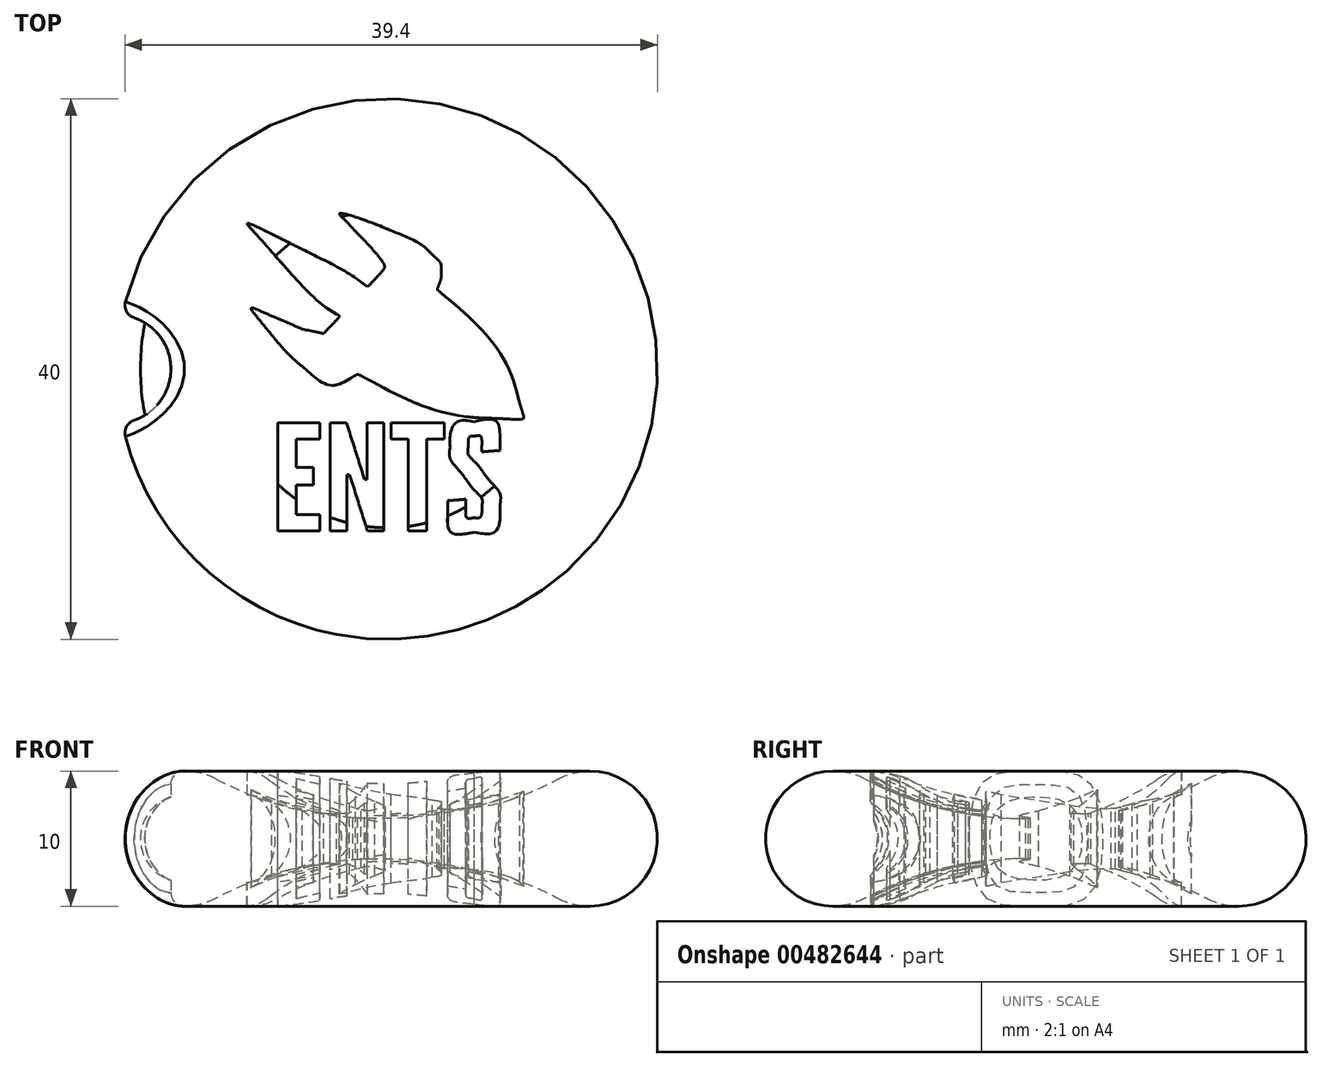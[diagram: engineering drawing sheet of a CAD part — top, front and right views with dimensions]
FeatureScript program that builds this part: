
annotation { "Feature Type Name" : "Feature", "Feature Type Description" : "" }
export const myFeature = defineFeature(function(context is Context, id is Id, definition is map)
    precondition{}
    {
        {
            var Q0;
            Q0=qCreatedBy(makeId("Front.planeOp"),FACE);
            var sketch = newSketch(context, id + "F0", { "sketchPlane" : qUnion([Q0])});
            skArc(sketch, "E0", {"start": v(-12.65, 5.91) * mm, "mid": v(-20, 1.5) * mm, "end": v(-12.65, -2.91) * mm});
            skArc(sketch, "E1", {"start": v(-12.65, 5.91) * mm, "mid": v(-6.52, 3.62) * mm, "end": v(0, 3) * mm});
            skLineSegment(sketch, "E2", {"start": v(0, 1.5) * mm, "end": v(-20, 1.5) * mm, "construction": true});
            skArc(sketch, "E3.MirrorCS", {"start": v(-12.65, -2.91) * mm, "mid": v(-6.52, -0.62) * mm, "end": v(0, 0) * mm});
            skLineSegment(sketch, "E4", {"start": v(0, 3) * mm, "end": v(0, 0) * mm});
            skSolve(sketch);
        }
        {
            var Q0;
            Q0=makeQuery(id+"F0.imprint","IMPRINT",FACE,{"disambiguationData":[TD([[makeQuery(id+"F0.imprint","IMPRINT",EDGE,{"derivedFrom":sQuery(id+"F0.wireOp",EDGE,"E0")}),1.0]])]});
            var Q1;
            Q1=sQuery(id+"F0.wireOp",EDGE,"E4");
            revolve(context, id + "F1", {"entities" : qUnion([Q0]), "axis" : qUnion([Q1]), "revolveType" : RevolveType.FULL});
        }
        {
            var Q0;
            Q0=qCreatedBy(makeId("Top.planeOp"),FACE);
            var sketch = newSketch(context, id + "F2", { "sketchPlane" : qUnion([Q0])});
            skCircle(sketch, "E5", {"center": v(-20, 0) * mm, "radius": 4 * mm});
            skSolve(sketch);
        }
        {
            var Q0;
            Q0=makeQuery(id+"F2.imprint","IMPRINT",FACE,{"disambiguationData":[TD([[makeQuery(id+"F2.imprint","IMPRINT",EDGE,{"derivedFrom":sQuery(id+"F2.wireOp",EDGE,"E5")}),1.0]])]});
            extrude(context, id + "F3", {"entities" : qUnion([Q0]), "operationType" : NewBodyOperationType.REMOVE, "endBound" : BoundingType.SYMMETRIC, "depth" : 25 * mm});
        }
        {
            var Q0;
            Q0=makeQuery(id+"F3.boolean.opBoolean","INTERSECT",EDGE,{"derivedFrom":[makeQuery(id+"F1.opRevolve","SWEPT_FACE",FACE,{"disambiguationData":[OSD([sQuery(id+"F0.wireOp",EDGE,"E0")])]}),makeQuery(id+"F3.opExtrude","SWEPT_FACE",FACE,{"disambiguationData":[OSD([sQuery(id+"F2.wireOp",EDGE,"E5")])]})]});
            fillet(context, id + "F4", {"entities" : qUnion([Q0]), "radius" : 1 * mm, "tangentPropagation" : true, "allowEdgeOverflow" : false});
        }
        {
            var Q0;
            Q0=qCreatedBy(makeId("Top.planeOp"),FACE);
            cPlane(context, id + "F5", {"entities" : qUnion([Q0]), "cplaneType" : CPlaneType.OFFSET, "offset" : 10 * mm, "width" : 150 * mm, "height" : 150 * mm});
        }
        {
            var Q0;
            Q0=qCreatedBy(id+"F5.planeOp",FACE);
            var sketch = newSketch(context, id + "F6", { "sketchPlane" : qUnion([Q0])});
            skFitSpline(sketch, "E6", {"points": [v(6.26, -0.16) * mm, v(5.7, -0.77) * mm, v(4.66, -0.87) * mm, v(3.96, -0.38) * mm], "construction": true});
            skFitSpline(sketch, "E7", {"points": [v(3.96, -0.38) * mm, v(3.25, 0.1) * mm, v(3.14, 1) * mm, v(3.7, 1.6) * mm], "construction": true});
            skFitSpline(sketch, "E8", {"points": [v(3.7, 1.6) * mm, v(4.26, 2.21) * mm, v(5.3, 2.31) * mm, v(6, 1.82) * mm], "construction": true});
            skFitSpline(sketch, "E9", {"points": [v(6, 1.82) * mm, v(6.7, 1.34) * mm, v(6.82, 0.45) * mm, v(6.26, -0.16) * mm], "construction": true});
            skLineSegment(sketch, "E10", {"start": v(-8.08, -3.99) * mm, "end": v(-4.97, -3.99) * mm});
            skLineSegment(sketch, "E11", {"start": v(-4.97, -3.99) * mm, "end": v(-4.97, -5.2) * mm});
            skLineSegment(sketch, "E12", {"start": v(-4.97, -5.2) * mm, "end": v(-6.72, -5.2) * mm});
            skLineSegment(sketch, "E13", {"start": v(-6.72, -5.2) * mm, "end": v(-6.72, -7.3) * mm});
            skLineSegment(sketch, "E14", {"start": v(-6.72, -7.3) * mm, "end": v(-5.46, -7.3) * mm});
            skLineSegment(sketch, "E15", {"start": v(-5.46, -7.3) * mm, "end": v(-5.46, -8.58) * mm});
            skLineSegment(sketch, "E16", {"start": v(-5.46, -8.58) * mm, "end": v(-6.72, -8.58) * mm});
            skLineSegment(sketch, "E17", {"start": v(-6.72, -8.58) * mm, "end": v(-6.72, -10.78) * mm});
            skLineSegment(sketch, "E18", {"start": v(-6.72, -10.78) * mm, "end": v(-4.97, -10.78) * mm});
            skLineSegment(sketch, "E19", {"start": v(-4.97, -10.78) * mm, "end": v(-4.97, -11.99) * mm});
            skLineSegment(sketch, "E20", {"start": v(-4.97, -11.99) * mm, "end": v(-8.08, -11.99) * mm});
            skLineSegment(sketch, "E21", {"start": v(-8.08, -11.99) * mm, "end": v(-8.08, -3.99) * mm});
            skLineSegment(sketch, "E22", {"start": v(-2.96, -7.82) * mm, "end": v(-2.96, -11.99) * mm});
            skLineSegment(sketch, "E23", {"start": v(-2.96, -11.99) * mm, "end": v(-4.21, -11.99) * mm});
            skLineSegment(sketch, "E24", {"start": v(-4.21, -11.99) * mm, "end": v(-4.21, -3.99) * mm});
            skLineSegment(sketch, "E25", {"start": v(-4.21, -3.99) * mm, "end": v(-3, -3.99) * mm});
            skLineSegment(sketch, "E26", {"start": v(-3, -3.99) * mm, "end": v(-1.68, -8.16) * mm});
            skLineSegment(sketch, "E27", {"start": v(-1.49, -8.16) * mm, "end": v(-1.49, -3.99) * mm});
            skLineSegment(sketch, "E28", {"start": v(-1.49, -3.99) * mm, "end": v(-0.24, -3.99) * mm});
            skLineSegment(sketch, "E29", {"start": v(-0.24, -3.99) * mm, "end": v(-0.24, -11.99) * mm});
            skLineSegment(sketch, "E30", {"start": v(-0.24, -11.99) * mm, "end": v(-1.45, -11.99) * mm});
            skLineSegment(sketch, "E31", {"start": v(-1.45, -11.99) * mm, "end": v(-2.77, -7.82) * mm});
            skFitSpline(sketch, "E32", {"points": [v(6.44, -3.9) * mm, v(8.08, -3.87) * mm, v(8.35, -5.13) * mm, v(8.35, -6.02) * mm]});
            skLineSegment(sketch, "E33", {"start": v(0.29, -5.2) * mm, "end": v(0.29, -3.99) * mm});
            skLineSegment(sketch, "E34", {"start": v(0.29, -3.99) * mm, "end": v(4.22, -3.99) * mm});
            skLineSegment(sketch, "E35", {"start": v(4.22, -3.99) * mm, "end": v(4.22, -5.2) * mm});
            skLineSegment(sketch, "E36", {"start": v(4.22, -5.2) * mm, "end": v(2.94, -5.2) * mm});
            skLineSegment(sketch, "E37", {"start": v(2.94, -5.2) * mm, "end": v(2.94, -11.99) * mm});
            skLineSegment(sketch, "E38", {"start": v(2.94, -11.99) * mm, "end": v(1.58, -11.99) * mm});
            skLineSegment(sketch, "E39", {"start": v(1.58, -11.99) * mm, "end": v(1.58, -5.2) * mm});
            skLineSegment(sketch, "E40", {"start": v(1.58, -5.2) * mm, "end": v(0.29, -5.2) * mm});
            skFitSpline(sketch, "E41", {"points": [v(7, -6.13) * mm, v(7, -5.6) * mm, v(6.92, -4.98) * mm, v(6.47, -4.98) * mm]});
            skFitSpline(sketch, "E42", {"points": [v(6.47, -4.98) * mm, v(6.11, -5) * mm, v(6, -5.32) * mm, v(6, -5.77) * mm]});
            skFitSpline(sketch, "E43", {"points": [v(6, -5.77) * mm, v(6, -6.32) * mm, v(6.54, -6.93) * mm, v(7.07, -7.6) * mm]});
            skFitSpline(sketch, "E44", {"points": [v(7.07, -7.6) * mm, v(7.7, -8.4) * mm, v(8.35, -9.2) * mm, v(8.35, -10.06) * mm]});
            skFitSpline(sketch, "E45", {"points": [v(8.35, -10.06) * mm, v(8.35, -11.13) * mm, v(7.94, -12.08) * mm, v(6.46, -12.08) * mm]});
            skFitSpline(sketch, "E46", {"points": [v(6.46, -12.08) * mm, v(4.7, -12.08) * mm, v(4.48, -10.93) * mm, v(4.48, -9.75) * mm]});
            skLineSegment(sketch, "E47", {"start": v(8.35, -6.02) * mm, "end": v(7, -6.13) * mm});
            skFitSpline(sketch, "E48", {"points": [v(5.81, -9.64) * mm, v(5.81, -10.3) * mm, v(5.89, -11) * mm, v(6.46, -11) * mm]});
            skFitSpline(sketch, "E49", {"points": [v(6.46, -11) * mm, v(6.86, -11) * mm, v(7.01, -10.62) * mm, v(7.01, -10.12) * mm]});
            skFitSpline(sketch, "E50", {"points": [v(7.01, -10.12) * mm, v(7.01, -9.58) * mm, v(6.43, -8.94) * mm, v(5.91, -8.27) * mm]});
            skFitSpline(sketch, "E51", {"points": [v(5.91, -8.27) * mm, v(5.27, -7.45) * mm, v(4.66, -6.63) * mm, v(4.66, -5.77) * mm]});
            skFitSpline(sketch, "E52", {"points": [v(4.66, -5.77) * mm, v(4.66, -4.9) * mm, v(5.16, -3.92) * mm, v(6.44, -3.9) * mm]});
            skLineSegment(sketch, "E53", {"start": v(4.48, -9.75) * mm, "end": v(5.81, -9.64) * mm});
            skLineSegment(sketch, "E54", {"start": v(-2.96, -7.82) * mm, "end": v(-2.77, -7.82) * mm});
            skLineSegment(sketch, "E55", {"start": v(-1.68, -8.16) * mm, "end": v(-1.49, -8.16) * mm});
            skSolve(sketch);
        }
        {
            var Q0;
            Q0 = qSketchRegion(id + "F6", true);
            extrude(context, id + "F7", {"entities" : qUnion([Q0]), "operationType" : NewBodyOperationType.REMOVE, "oppositeDirection" : true, "depth" : 25 * mm});
        }
        {
            var Q0;
            Q0=qCreatedBy(id+"F5.planeOp",FACE);
            var sketch = newSketch(context, id + "F8", { "sketchPlane" : qUnion([Q0])});
            skFitSpline(sketch, "E56", {"points": [v(-3.48, 11.5) * mm, v(-3.5, 11.51) * mm, v(-3.52, 11.5) * mm, v(-3.53, 11.5) * mm]});
            skFitSpline(sketch, "E57", {"points": [v(-3.53, 11.5) * mm, v(-3.54, 11.49) * mm, v(-3.01, 10.9) * mm, v(-2.35, 10.2) * mm]});
            skFitSpline(sketch, "E58", {"points": [v(-2.35, 10.2) * mm, v(-1.69, 9.5) * mm, v(-1.04, 8.8) * mm, v(-0.9, 8.65) * mm]});
            skFitSpline(sketch, "E59", {"points": [v(-0.9, 8.65) * mm, v(-0.66, 8.37) * mm, v(-0.17, 7.59) * mm, v(-0.2, 7.51) * mm]});
            skFitSpline(sketch, "E60", {"points": [v(-0.2, 7.51) * mm, v(-0.22, 7.43) * mm, v(-1.43, 6.13) * mm, v(-1.48, 6.13) * mm]});
            skFitSpline(sketch, "E61", {"points": [v(-1.48, 6.13) * mm, v(-1.5, 6.13) * mm, v(-1.7, 6.26) * mm, v(-1.93, 6.42) * mm]});
            skFitSpline(sketch, "E62", {"points": [v(-1.93, 6.42) * mm, v(-2.67, 6.96) * mm, v(-4.18, 7.81) * mm, v(-6.1, 8.77) * mm]});
            skFitSpline(sketch, "E63", {"points": [v(-6.1, 8.77) * mm, v(-7.7, 9.57) * mm, v(-10.25, 10.78) * mm, v(-10.34, 10.78) * mm]});
            skFitSpline(sketch, "E64", {"points": [v(-10.34, 10.78) * mm, v(-10.38, 10.78) * mm, v(-9.65, 9.92) * mm, v(-8.6, 8.73) * mm]});
            skFitSpline(sketch, "E65", {"points": [v(-8.6, 8.73) * mm, v(-6.63, 6.53) * mm, v(-4.68, 4.65) * mm, v(-3.73, 4.06) * mm]});
            skFitSpline(sketch, "E66", {"points": [v(-3.73, 4.06) * mm, v(-3.63, 4) * mm, v(-3.54, 3.92) * mm, v(-3.54, 3.9) * mm]});
            skFitSpline(sketch, "E67", {"points": [v(-3.54, 3.9) * mm, v(-3.54, 3.86) * mm, v(-3.8, 3.56) * mm, v(-4.12, 3.23) * mm]});
            skFitSpline(sketch, "E68", {"points": [v(-5.5, 2.8) * mm, v(-6.26, 2.96) * mm, v(-6.36, 3) * mm, v(-8.14, 3.76) * mm]});
            skFitSpline(sketch, "E69", {"points": [v(-8.14, 3.76) * mm, v(-9.16, 4.2) * mm, v(-10, 4.54) * mm, v(-10.03, 4.53) * mm]});
            skFitSpline(sketch, "E70", {"points": [v(-10.03, 4.53) * mm, v(-10.08, 4.52) * mm, v(-9.22, 3.35) * mm, v(-8.53, 2.5) * mm]});
            skFitSpline(sketch, "E71", {"points": [v(-8.53, 2.5) * mm, v(-7.83, 1.66) * mm, v(-6.86, 0.66) * mm, v(-6.28, 0.2) * mm]});
            skFitSpline(sketch, "E72", {"points": [v(-6.28, 0.2) * mm, v(-4.8, -1) * mm, v(-3.8, -1.19) * mm, v(-2.52, -0.56) * mm]});
            skLineSegment(sketch, "E73", {"start": v(-4.12, 3.23) * mm, "end": v(-4.7, 2.62) * mm});
            skLineSegment(sketch, "E74", {"start": v(-4.7, 2.62) * mm, "end": v(-5.5, 2.8) * mm});
            skFitSpline(sketch, "E75", {"points": [v(-1.43, -0.76) * mm, v(1.95, -2.45) * mm, v(5.3, -3.46) * mm, v(8.27, -3.66) * mm]});
            skFitSpline(sketch, "E76", {"points": [v(8.27, -3.66) * mm, v(8.93, -3.7) * mm, v(10.03, -3.7) * mm, v(10.07, -3.66) * mm]});
            skFitSpline(sketch, "E77", {"points": [v(10.07, -3.66) * mm, v(10.1, -3.62) * mm, v(9.98, -3.1) * mm, v(9.8, -2.55) * mm]});
            skFitSpline(sketch, "E78", {"points": [v(9.8, -2.55) * mm, v(8.96, 0.1) * mm, v(6.9, 3) * mm, v(4.05, 5.58) * mm]});
            skLineSegment(sketch, "E79", {"start": v(-2.52, -0.56) * mm, "end": v(-2.17, -0.39) * mm});
            skLineSegment(sketch, "E80", {"start": v(-2.17, -0.39) * mm, "end": v(-1.43, -0.76) * mm});
            skFitSpline(sketch, "E81", {"points": [v(3.85, 6.3) * mm, v(3.97, 6.62) * mm, v(4, 6.78) * mm, v(4, 7.12) * mm]});
            skFitSpline(sketch, "E82", {"points": [v(4, 7.12) * mm, v(4, 7.69) * mm, v(3.86, 7.96) * mm, v(3.34, 8.46) * mm]});
            skFitSpline(sketch, "E83", {"points": [v(3.34, 8.46) * mm, v(2.7, 9.07) * mm, v(1.73, 9.64) * mm, v(0.3, 10.24) * mm]});
            skFitSpline(sketch, "E84", {"points": [v(0.3, 10.24) * mm, v(-0.88, 10.72) * mm, v(-3.14, 11.48) * mm, v(-3.48, 11.5) * mm]});
            skLineSegment(sketch, "E85", {"start": v(4.05, 5.58) * mm, "end": v(3.7, 5.9) * mm});
            skLineSegment(sketch, "E86", {"start": v(3.7, 5.9) * mm, "end": v(3.85, 6.3) * mm});
            skFitSpline(sketch, "E87", {"points": [v(4.4, 1.47) * mm, v(5.03, 1.51) * mm, v(5.58, 1.25) * mm, v(5.85, 0.78) * mm], "construction": true});
            skFitSpline(sketch, "E88", {"points": [v(5.85, 0.78) * mm, v(6.04, 0.44) * mm, v(6.08, 0.17) * mm, v(5.98, -0.16) * mm], "construction": true});
            skFitSpline(sketch, "E89", {"points": [v(5.98, -0.16) * mm, v(5.82, -0.62) * mm, v(5.52, -0.91) * mm, v(5, -1.06) * mm], "construction": true});
            skFitSpline(sketch, "E90", {"points": [v(5, -1.06) * mm, v(3.86, -1.4) * mm, v(2.74, -0.5) * mm, v(3.06, 0.52) * mm], "construction": true});
            skFitSpline(sketch, "E91", {"points": [v(3.06, 0.52) * mm, v(3.23, 1.07) * mm, v(3.75, 1.43) * mm, v(4.4, 1.47) * mm], "construction": true});
            skSolve(sketch);
        }
        {
            var Q0;
            Q0 = qSketchRegion(id + "F8", true);
            extrude(context, id + "F9", {"entities" : qUnion([Q0]), "operationType" : NewBodyOperationType.REMOVE, "oppositeDirection" : true, "depth" : 25 * mm});
        }
        {
            var Q0;
            Q0=qCreatedBy(makeId("Front.planeOp"),FACE);
            var sketch = newSketch(context, id + "F10", { "sketchPlane" : qUnion([Q0])});
            skCircle(sketch, "E92", {"center": v(-15, 1.5) * mm, "radius": 3.25 * mm});
            skSolve(sketch);
        }
        {
            var Q0;
            Q0 = qSketchRegion(id + "F10", true);
            var Q1;
            Q1=sQuery(id+"F0.wireOp",EDGE,"E4");
            revolve(context, id + "F11", {"operationType" : NewBodyOperationType.ADD, "entities" : qUnion([Q0]), "axis" : qUnion([Q1]), "revolveType" : RevolveType.FULL});
        }
    });
